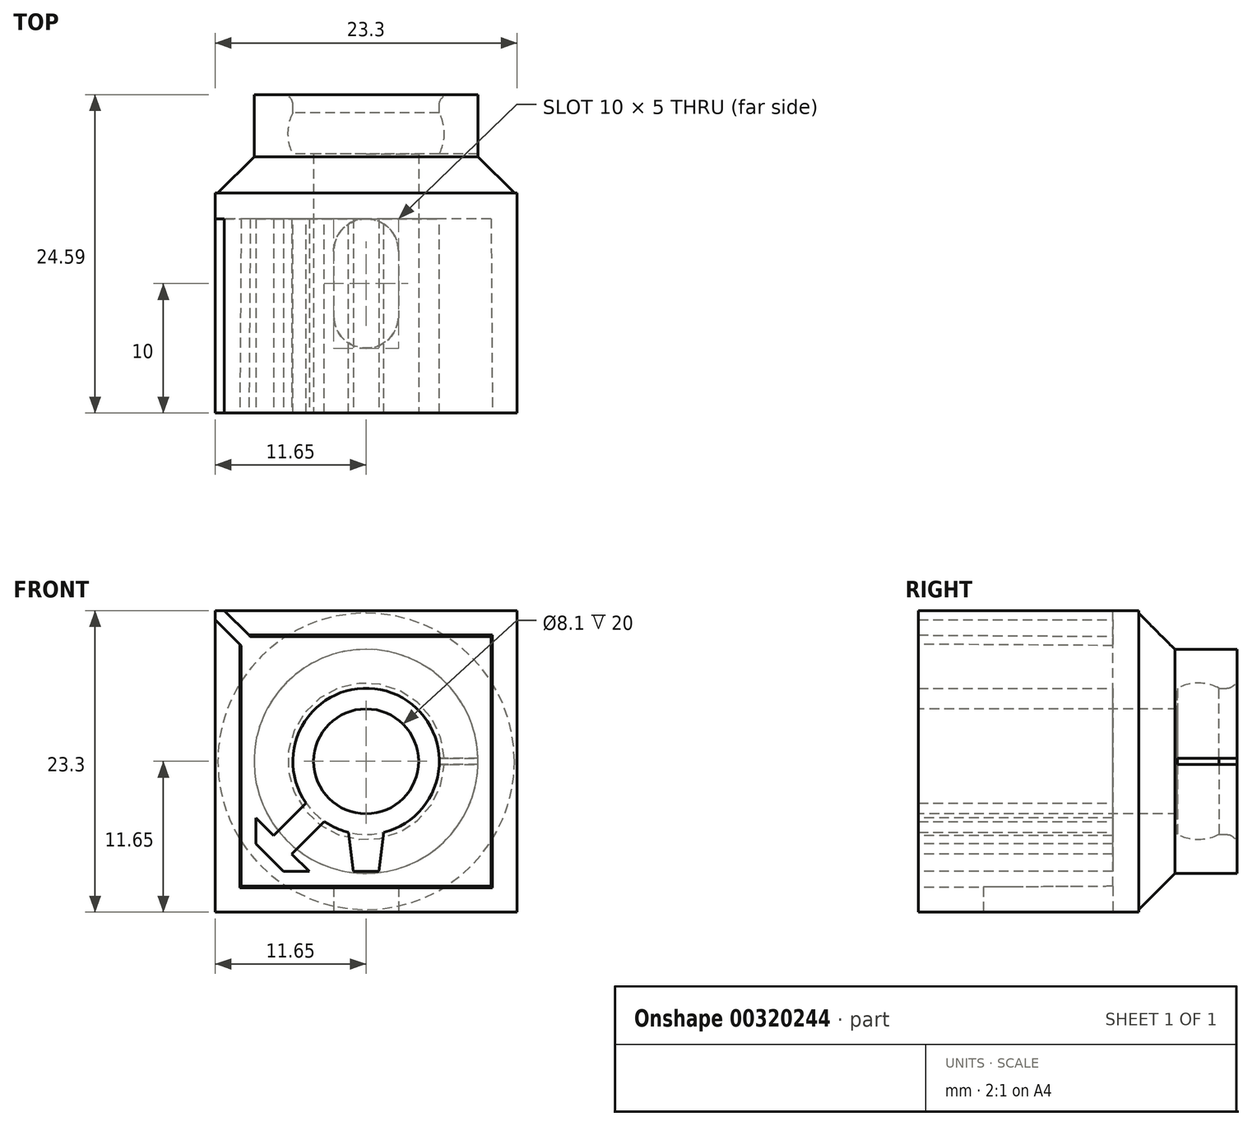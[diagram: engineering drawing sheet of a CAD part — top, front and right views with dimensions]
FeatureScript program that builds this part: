
annotation { "Feature Type Name" : "Feature", "Feature Type Description" : "" }
export const myFeature = defineFeature(function(context is Context, id is Id, definition is map)
    precondition{}
    {
        {
            var Q0;
            Q0=qCreatedBy(makeId("Front.planeOp"),FACE);
            var sketch = newSketch(context, id + "F0", { "sketchPlane" : qUnion([Q0])});
            skLineSegment(sketch, "E0.bottom", {"start": v(9.5, -9.5) * mm, "end": v(-9.5, -9.5) * mm, "construction": true});
            skLineSegment(sketch, "E0.top", {"start": v(9.5, 9.5) * mm, "end": v(-9.5, 9.5) * mm, "construction": true});
            skLineSegment(sketch, "E0.left", {"start": v(9.5, -9.5) * mm, "end": v(9.5, 9.5) * mm, "construction": true});
            skLineSegment(sketch, "E0.right", {"start": v(-9.5, -9.5) * mm, "end": v(-9.5, 9.5) * mm, "construction": true});
            skPoint(sketch, "E0.middle", {"position": v(0, 0) * mm});
            skLineSegment(sketch, "E1.0", {"start": v(8.5, 8.5) * mm, "end": v(-8.5, 8.5) * mm, "construction": true});
            skLineSegment(sketch, "E1.1", {"start": v(8.5, -8.5) * mm, "end": v(8.5, 8.5) * mm, "construction": true});
            skLineSegment(sketch, "E1.2", {"start": v(8.5, -8.5) * mm, "end": v(-8.5, -8.5) * mm, "construction": true});
            skLineSegment(sketch, "E1.3", {"start": v(-8.5, -8.5) * mm, "end": v(-8.5, 8.5) * mm, "construction": true});
            skSolve(sketch);
        }
        {
            var Q0;
            Q0=qCreatedBy(makeId("Front.planeOp"),FACE);
            var sketch = newSketch(context, id + "F1", { "sketchPlane" : qUnion([Q0])});
            skLineSegment(sketch, "E2.0", {"start": v(8.4, 8.4) * mm, "end": v(-8.4, 8.4) * mm});
            skLineSegment(sketch, "E2.1", {"start": v(8.4, -8.4) * mm, "end": v(8.4, 8.4) * mm});
            skLineSegment(sketch, "E2.2", {"start": v(8.4, -8.4) * mm, "end": v(-8.4, -8.4) * mm});
            skLineSegment(sketch, "E2.3", {"start": v(-8.4, -8.4) * mm, "end": v(-8.4, 8.4) * mm});
            skLineSegment(sketch, "E3.0", {"start": v(9.65, 9.65) * mm, "end": v(-9.65, 9.65) * mm});
            skLineSegment(sketch, "E3.1", {"start": v(9.65, -9.65) * mm, "end": v(9.65, 9.65) * mm});
            skLineSegment(sketch, "E3.2", {"start": v(9.65, -9.65) * mm, "end": v(-9.65, -9.65) * mm});
            skLineSegment(sketch, "E3.3", {"start": v(-9.65, -9.65) * mm, "end": v(-9.65, 9.65) * mm});
            skLineSegment(sketch, "E4.0", {"start": v(11.65, 11.65) * mm, "end": v(-11.65, 11.65) * mm});
            skLineSegment(sketch, "E4.1", {"start": v(11.65, -11.65) * mm, "end": v(11.65, 11.65) * mm});
            skLineSegment(sketch, "E4.2", {"start": v(11.65, -11.65) * mm, "end": v(-11.65, -11.65) * mm});
            skLineSegment(sketch, "E4.3", {"start": v(-11.65, -11.65) * mm, "end": v(-11.65, 11.65) * mm});
            skLineSegment(sketch, "E5.0", {"start": v(6.4, 6.4) * mm, "end": v(-6.4, 6.4) * mm});
            skLineSegment(sketch, "E5.1", {"start": v(6.4, -6.4) * mm, "end": v(6.4, 6.4) * mm});
            skLineSegment(sketch, "E5.2", {"start": v(6.4, -6.4) * mm, "end": v(-6.4, -6.4) * mm});
            skLineSegment(sketch, "E5.3", {"start": v(-6.4, -6.4) * mm, "end": v(-6.4, 6.4) * mm});
            skSolve(sketch);
        }
        {
            var Q0;
            Q0=makeQuery(id+"F1.imprint","IMPRINT",FACE,{"disambiguationData":[TD([[makeQuery(id+"F1.imprint","IMPRINT",EDGE,{"derivedFrom":sQuery(id+"F1.wireOp",EDGE,"E3.0")}),-1.0]])]});
            extrude(context, id + "F2", {"entities" : qUnion([Q0]), "oppositeDirection" : true, "depth" : 25 * mm});
        }
        {
            var Q0;
            Q0=makeQuery(id+"F2.opExtrude","CAP_FACE",FACE,{"disambiguationData":[OSD([sQuery(id+"F1.wireOp",EDGE,"E3.0"),sQuery(id+"F1.wireOp",EDGE,"E3.1"),sQuery(id+"F1.wireOp",EDGE,"E3.2"),sQuery(id+"F1.wireOp",EDGE,"E3.3"),sQuery(id+"F1.wireOp",EDGE,"E4.0"),sQuery(id+"F1.wireOp",EDGE,"E4.1"),sQuery(id+"F1.wireOp",EDGE,"E4.2"),sQuery(id+"F1.wireOp",EDGE,"E4.3")])],"isStart":true});
            var sketch = newSketch(context, id + "F3", { "sketchPlane" : qUnion([Q0])});
            skLineSegment(sketch, "E6.0.0", {"start": v(-11.65, 11.65) * mm, "end": v(-11.65, -11.65) * mm});
            skLineSegment(sketch, "E6.0.1", {"start": v(-11.65, -11.65) * mm, "end": v(11.65, -11.65) * mm});
            skLineSegment(sketch, "E6.0.2", {"start": v(11.65, -11.65) * mm, "end": v(11.65, 11.65) * mm});
            skLineSegment(sketch, "E6.0.3", {"start": v(11.65, 11.65) * mm, "end": v(-11.65, 11.65) * mm});
            skSolve(sketch);
        }
        {
            var Q0;
            Q0=qSketchRegion(id+"F3",true);
            extrude(context, id + "F4", {"entities" : qUnion([Q0]), "operationType" : NewBodyOperationType.ADD, "oppositeDirection" : true, "depth" : 3 * mm});
        }
        {
            var Q0;
            Q0=makeQuery(id+"F4.boolean.opBoolean","MERGE",FACE,{"derivedFrom":[makeQuery(id+"F2.opExtrude","CAP_FACE",FACE,{"disambiguationData":[OSD([sQuery(id+"F1.wireOp",EDGE,"E2.0"),sQuery(id+"F1.wireOp",EDGE,"E2.1"),sQuery(id+"F1.wireOp",EDGE,"E2.2"),sQuery(id+"F1.wireOp",EDGE,"E2.3"),sQuery(id+"F1.wireOp",EDGE,"E5.0"),sQuery(id+"F1.wireOp",EDGE,"E5.1"),sQuery(id+"F1.wireOp",EDGE,"E5.2"),sQuery(id+"F1.wireOp",EDGE,"E5.3")])],"isStart":true}),makeQuery(id+"F2.opExtrude","CAP_FACE",FACE,{"disambiguationData":[OSD([sQuery(id+"F1.wireOp",EDGE,"E3.0"),sQuery(id+"F1.wireOp",EDGE,"E3.1"),sQuery(id+"F1.wireOp",EDGE,"E3.2"),sQuery(id+"F1.wireOp",EDGE,"E3.3"),sQuery(id+"F1.wireOp",EDGE,"E4.0"),sQuery(id+"F1.wireOp",EDGE,"E4.1"),sQuery(id+"F1.wireOp",EDGE,"E4.2"),sQuery(id+"F1.wireOp",EDGE,"E4.3")])],"isStart":true}),makeQuery(id+"F4.opExtrude","CAP_FACE",FACE,{"disambiguationData":[OSD([sQuery(id+"F3.wireOp",EDGE,"E6.0.0"),sQuery(id+"F3.wireOp",EDGE,"E6.0.1"),sQuery(id+"F3.wireOp",EDGE,"E6.0.2"),sQuery(id+"F3.wireOp",EDGE,"E6.0.3")])],"isStart":true})]});
            var sketch = newSketch(context, id + "F5", { "sketchPlane" : qUnion([Q0])});
            skCircle(sketch, "E7", {"center": v(0, 0) * mm, "radius": 4.05 * mm});
            skSolve(sketch);
        }
        {
            var Q0;
            Q0=qSketchRegion(id+"F5",true);
            extrude(context, id + "F6", {"entities" : qUnion([Q0]), "operationType" : NewBodyOperationType.REMOVE, "endBound" : BoundingType.THROUGH_ALL, "oppositeDirection" : true, "depth" : 25 * mm});
        }
        {
            var Q0;
            Q0=qCreatedBy(makeId("Right.planeOp"),FACE);
            var sketch = newSketch(context, id + "F7", { "sketchPlane" : qUnion([Q0])});
            skLineSegment(sketch, "E8.bottom", {"start": v(3, -4.05) * mm, "end": v(20, -4.05) * mm});
            skLineSegment(sketch, "E8.top", {"start": v(3, -5.65) * mm, "end": v(20, -5.65) * mm});
            skLineSegment(sketch, "E8.left", {"start": v(3, -4.05) * mm, "end": v(3, -5.65) * mm});
            skLineSegment(sketch, "E8.right", {"start": v(20, -4.05) * mm, "end": v(20, -5.65) * mm});
            skArc(sketch, "E9", {"start": v(20, -5.65) * mm, "mid": v(21.6, -6.05) * mm, "end": v(23.2, -5.65) * mm});
            skLineSegment(sketch, "E10", {"start": v(23.2, -5.65) * mm, "end": v(26.09, -5.65) * mm});
            skArc(sketch, "E11.0", {"start": v(17.11, -5.65) * mm, "mid": v(21.6, -8.05) * mm, "end": v(26.09, -5.65) * mm});
            skLineSegment(sketch, "E12", {"start": v(24.82, -8.05) * mm, "end": v(16.07, -8.05) * mm, "construction": true});
            skSolve(sketch);
        }
        {
            var Q0;
            Q0=qSketchRegion(id+"F7",true);
            var Q1;
            Q1=makeQuery(id+"F6.boolean.opBoolean","INTERSECT",EDGE,{"derivedFrom":[makeQuery(id+"F4.opExtrude","CAP_FACE",FACE,{"disambiguationData":[OSD([sQuery(id+"F3.wireOp",EDGE,"E6.0.0"),sQuery(id+"F3.wireOp",EDGE,"E6.0.1"),sQuery(id+"F3.wireOp",EDGE,"E6.0.2"),sQuery(id+"F3.wireOp",EDGE,"E6.0.3")])],"isStart":false}),makeQuery(id+"F6.opExtrude","SWEPT_FACE",FACE,{"disambiguationData":[OSD([sQuery(id+"F5.wireOp",EDGE,"E7")])]})]});
            revolve(context, id + "F8", {"operationType" : NewBodyOperationType.ADD, "entities" : qUnion([Q0]), "axis" : qUnion([Q1]), "revolveType" : RevolveType.FULL});
        }
        {
            var Q0;
            Q0=makeQuery(id+"F2.opExtrude","CAP_FACE",FACE,{"disambiguationData":[OSD([sQuery(id+"F1.wireOp",EDGE,"E3.0"),sQuery(id+"F1.wireOp",EDGE,"E3.1"),sQuery(id+"F1.wireOp",EDGE,"E3.2"),sQuery(id+"F1.wireOp",EDGE,"E3.3"),sQuery(id+"F1.wireOp",EDGE,"E4.0"),sQuery(id+"F1.wireOp",EDGE,"E4.1"),sQuery(id+"F1.wireOp",EDGE,"E4.2"),sQuery(id+"F1.wireOp",EDGE,"E4.3")])],"isStart":false});
            cPlane(context, id + "F9", {"entities" : qUnion([Q0]), "cplaneType" : CPlaneType.OFFSET, "offset" : 8 * mm, "oppositeDirection" : true, "width" : 150 * mm, "height" : 150 * mm});
        }
        {
            var Q0;
            Q0=qCreatedBy(id+"F9.planeOp",FACE);
            var sketch = newSketch(context, id + "F10", { "sketchPlane" : qUnion([Q0])});
            skLineSegment(sketch, "E13.0.0", {"start": v(11.65, -11.65) * mm, "end": v(11.65, 11.65) * mm});
            skLineSegment(sketch, "E13.0.1", {"start": v(11.65, 11.65) * mm, "end": v(-11.65, 11.65) * mm});
            skLineSegment(sketch, "E13.0.2", {"start": v(-11.65, 11.65) * mm, "end": v(-11.65, -11.65) * mm});
            skLineSegment(sketch, "E13.0.3", {"start": v(-11.65, -11.65) * mm, "end": v(11.65, -11.65) * mm});
            skSolve(sketch);
        }
        {
            var Q0;
            Q0=qSketchRegion(id+"F10",true);
            extrude(context, id + "F11", {"entities" : qUnion([Q0]), "oppositeDirection" : true, "depth" : 2 * mm});
        }
        {
            var Q0;
            Q0=makeQuery(id+"F2.opExtrude","SWEPT_BODY",BODY,{"disambiguationData":[OSD([sQuery(id+"F1.wireOp",EDGE,"E3.0"),sQuery(id+"F1.wireOp",EDGE,"E3.1"),sQuery(id+"F1.wireOp",EDGE,"E3.2"),sQuery(id+"F1.wireOp",EDGE,"E3.3"),sQuery(id+"F1.wireOp",EDGE,"E4.0"),sQuery(id+"F1.wireOp",EDGE,"E4.1"),sQuery(id+"F1.wireOp",EDGE,"E4.2"),sQuery(id+"F1.wireOp",EDGE,"E4.3")])]});
            var Q1;
            Q1=makeQuery(id+"F11.opExtrude","SWEPT_BODY",BODY,{"disambiguationData":[OSD([sQuery(id+"F10.wireOp",EDGE,"E13.0.0"),sQuery(id+"F10.wireOp",EDGE,"E13.0.1"),sQuery(id+"F10.wireOp",EDGE,"E13.0.2"),sQuery(id+"F10.wireOp",EDGE,"E13.0.3")])]});
            booleanBodies(context, id + "F12", {"operationType" : BooleanOperationType.UNION, "tools" : qUnion([Q0, Q1])});
        }
        {
            var Q0;
            Q0=makeQuery(id+"F12.opBoolean","SPLIT",FACE,{"disambiguationData":[TD([makeQuery(id+"F6.boolean.opBoolean","COPY",FACE,{"derivedFrom":makeQuery(id+"F6.opExtrude","SWEPT_FACE",FACE,{"disambiguationData":[OSD([sQuery(id+"F5.wireOp",EDGE,"E7")])]})})])],"derivedFrom":makeQuery(id+"F11.opExtrude","CAP_FACE",FACE,{"disambiguationData":[OSD([sQuery(id+"F10.wireOp",EDGE,"E13.0.0"),sQuery(id+"F10.wireOp",EDGE,"E13.0.1"),sQuery(id+"F10.wireOp",EDGE,"E13.0.2"),sQuery(id+"F10.wireOp",EDGE,"E13.0.3")])],"isStart":true})});
            var sketch = newSketch(context, id + "F13", { "sketchPlane" : qUnion([Q0])});
            skCircle(sketch, "E14.0", {"center": v(0, 0) * mm, "radius": 4.05 * mm});
            skSolve(sketch);
        }
        {
            var Q0;
            Q0=qSketchRegion(id+"F13",true);
            extrude(context, id + "F14", {"entities" : qUnion([Q0]), "operationType" : NewBodyOperationType.REMOVE, "endBound" : BoundingType.THROUGH_ALL, "oppositeDirection" : true, "depth" : 25 * mm});
        }
        {
            var Q0;
            Q0=makeQuery(id+"F4.opExtrude","CAP_FACE",FACE,{"disambiguationData":[OSD([sQuery(id+"F3.wireOp",EDGE,"E6.0.0"),sQuery(id+"F3.wireOp",EDGE,"E6.0.1"),sQuery(id+"F3.wireOp",EDGE,"E6.0.2"),sQuery(id+"F3.wireOp",EDGE,"E6.0.3")])],"isStart":false});
            var sketch = newSketch(context, id + "F15", { "sketchPlane" : qUnion([Q0])});
            skLineSegment(sketch, "E15.0.0", {"start": v(-9.65, -9.65) * mm, "end": v(9.65, -9.65) * mm});
            skLineSegment(sketch, "E15.0.1", {"start": v(9.65, -9.65) * mm, "end": v(9.65, 9.65) * mm});
            skLineSegment(sketch, "E15.0.2", {"start": v(9.65, 9.65) * mm, "end": v(-9.65, 9.65) * mm});
            skLineSegment(sketch, "E15.0.3", {"start": v(-9.65, 9.65) * mm, "end": v(-9.65, -9.65) * mm});
            skCircle(sketch, "E16.0", {"center": v(0, 0) * mm, "radius": 5.65 * mm});
            skSolve(sketch);
        }
        {
            var Q0;
            Q0=qSketchRegion(id+"F15",true);
            extrude(context, id + "F16", {"entities" : qUnion([Q0]), "operationType" : NewBodyOperationType.REMOVE, "endBound" : BoundingType.THROUGH_ALL, "oppositeDirection" : true, "depth" : 25 * mm});
        }
        {
            var Q0;
            Q0=makeQuery(id+"F12.opBoolean","SPLIT",FACE,{"disambiguationData":[TD([makeQuery(id+"F2.opExtrude","SWEPT_FACE",FACE,{"disambiguationData":[OSD([sQuery(id+"F1.wireOp",EDGE,"E3.0")])]})])],"derivedFrom":makeQuery(id+"F11.opExtrude","CAP_FACE",FACE,{"disambiguationData":[OSD([sQuery(id+"F10.wireOp",EDGE,"E13.0.0"),sQuery(id+"F10.wireOp",EDGE,"E13.0.1"),sQuery(id+"F10.wireOp",EDGE,"E13.0.2"),sQuery(id+"F10.wireOp",EDGE,"E13.0.3")])],"isStart":false})});
            var sketch = newSketch(context, id + "F17", { "sketchPlane" : qUnion([Q0])});
            skLineSegment(sketch, "E17.0", {"start": v(9.5, -9.5) * mm, "end": v(-9.5, -9.5) * mm});
            skLineSegment(sketch, "E17.1", {"start": v(9.5, 9.5) * mm, "end": v(-9.5, 9.5) * mm});
            skLineSegment(sketch, "E17.2", {"start": v(9.5, -9.5) * mm, "end": v(9.5, 9.5) * mm});
            skLineSegment(sketch, "E17.3", {"start": v(-9.5, -9.5) * mm, "end": v(-9.5, 9.5) * mm});
            skPoint(sketch, "E17.4", {"position": v(0, 0) * mm});
            skLineSegment(sketch, "E17.5", {"start": v(8.5, 8.5) * mm, "end": v(-8.5, 8.5) * mm});
            skLineSegment(sketch, "E17.6", {"start": v(8.5, -8.5) * mm, "end": v(8.5, 8.5) * mm});
            skLineSegment(sketch, "E17.7", {"start": v(8.5, -8.5) * mm, "end": v(-8.5, -8.5) * mm});
            skLineSegment(sketch, "E17.8", {"start": v(-8.5, -8.5) * mm, "end": v(-8.5, 8.5) * mm});
            skSolve(sketch);
        }
        {
            var Q0;
            {var subQ0=sQuery(id+"F1.wireOp",EDGE,"E4.3");var subQ1=sQuery(id+"F1.wireOp",EDGE,"E4.2");var subQ2=sQuery(id+"F1.wireOp",EDGE,"E4.1");var subQ3=sQuery(id+"F1.wireOp",EDGE,"E4.0");var subQ4=sQuery(id+"F1.wireOp",EDGE,"E3.0");var subQ5=sQuery(id+"F1.wireOp",EDGE,"E3.3");var subQ6=sQuery(id+"F1.wireOp",EDGE,"E3.1");var subQ7=sQuery(id+"F1.wireOp",EDGE,"E3.2");Q0=makeQuery(id+"F16.boolean.opBoolean","SPLIT",FACE,{"disambiguationData":[TD([makeQuery(id+"F2.opExtrude","SWEPT_FACE",FACE,{"disambiguationData":[OSD([subQ4])]})])],"derivedFrom":makeQuery(id+"F4.boolean.opBoolean","MERGE",FACE,{"derivedFrom":[makeQuery(id+"F2.opExtrude","CAP_FACE",FACE,{"disambiguationData":[OSD([subQ4,subQ6,subQ7,subQ5,subQ3,subQ2,subQ1,subQ0])],"isStart":true}),makeQuery(id+"F4.opExtrude","CAP_FACE",FACE,{"disambiguationData":[OSD([sQuery(id+"F3.wireOp",EDGE,"E6.0.0"),sQuery(id+"F3.wireOp",EDGE,"E6.0.1"),sQuery(id+"F3.wireOp",EDGE,"E6.0.2"),sQuery(id+"F3.wireOp",EDGE,"E6.0.3")])],"isStart":true})]})});}
            var sketch = newSketch(context, id + "F18", { "sketchPlane" : qUnion([Q0])});
            skLineSegment(sketch, "E18", {"start": v(1.5, -4.5) * mm, "end": v(0.97, -8.5) * mm});
            skLineSegment(sketch, "E19", {"start": v(-0.97, -8.5) * mm, "end": v(-1.5, -4.5) * mm});
            skLineSegment(sketch, "E20", {"start": v(-1.5, -4.5) * mm, "end": v(1.5, -4.5) * mm});
            skLineSegment(sketch, "E21.0", {"start": v(8.5, -8.5) * mm, "end": v(-8.5, -8.5) * mm, "construction": true});
            skPoint(sketch, "E22.orphan", {"position": v(0, -15.9) * mm});
            skLineSegment(sketch, "E23", {"start": v(-0.97, -8.5) * mm, "end": v(0.97, -8.5) * mm});
            skSolve(sketch);
        }
        {
            var Q0;
            Q0=qSketchRegion(id+"F18",true);
            var Q1;
            Q1=makeQuery(id+"F12.opBoolean","SPLIT",FACE,{"disambiguationData":[TD([makeQuery(id+"F2.opExtrude","SWEPT_FACE",FACE,{"disambiguationData":[OSD([sQuery(id+"F1.wireOp",EDGE,"E3.0")])]})])],"derivedFrom":makeQuery(id+"F11.opExtrude","CAP_FACE",FACE,{"disambiguationData":[OSD([sQuery(id+"F10.wireOp",EDGE,"E13.0.0"),sQuery(id+"F10.wireOp",EDGE,"E13.0.1"),sQuery(id+"F10.wireOp",EDGE,"E13.0.2"),sQuery(id+"F10.wireOp",EDGE,"E13.0.3")])],"isStart":false})});
            extrude(context, id + "F19", {"entities" : qUnion([Q0]), "operationType" : NewBodyOperationType.ADD, "endBound" : BoundingType.UP_TO_SURFACE, "oppositeDirection" : true, "endBoundEntityFace" : qUnion([Q1]), "depth" : 25 * mm});
        }
        {
            var Q0;
            {var subQ0=sQuery(id+"F1.wireOp",EDGE,"E4.3");var subQ1=sQuery(id+"F1.wireOp",EDGE,"E4.2");var subQ2=sQuery(id+"F1.wireOp",EDGE,"E4.1");var subQ3=sQuery(id+"F1.wireOp",EDGE,"E4.0");var subQ4=sQuery(id+"F1.wireOp",EDGE,"E3.0");var subQ5=sQuery(id+"F1.wireOp",EDGE,"E3.3");var subQ6=sQuery(id+"F1.wireOp",EDGE,"E3.1");var subQ7=sQuery(id+"F1.wireOp",EDGE,"E3.2");Q0=makeQuery(id+"F16.boolean.opBoolean","SPLIT",FACE,{"disambiguationData":[TD([makeQuery(id+"F2.opExtrude","SWEPT_FACE",FACE,{"disambiguationData":[OSD([subQ4])]})])],"derivedFrom":makeQuery(id+"F4.boolean.opBoolean","MERGE",FACE,{"derivedFrom":[makeQuery(id+"F2.opExtrude","CAP_FACE",FACE,{"disambiguationData":[OSD([subQ4,subQ6,subQ7,subQ5,subQ3,subQ2,subQ1,subQ0])],"isStart":true}),makeQuery(id+"F4.opExtrude","CAP_FACE",FACE,{"disambiguationData":[OSD([sQuery(id+"F3.wireOp",EDGE,"E6.0.0"),sQuery(id+"F3.wireOp",EDGE,"E6.0.1"),sQuery(id+"F3.wireOp",EDGE,"E6.0.2"),sQuery(id+"F3.wireOp",EDGE,"E6.0.3")])],"isStart":true})]})});}
            var sketch = newSketch(context, id + "F20", { "sketchPlane" : qUnion([Q0])});
            skLineSegment(sketch, "E24", {"start": v(-6.38, -8.5) * mm, "end": v(-8.5, -6.38) * mm});
            skLineSegment(sketch, "E25.0", {"start": v(-8.5, -6.38) * mm, "end": v(-8.5, -4.38) * mm});
            skLineSegment(sketch, "E26.0", {"start": v(-4.38, -8.5) * mm, "end": v(-6.38, -8.5) * mm});
            skCircle(sketch, "E27.0", {"center": v(0, 0) * mm, "radius": 4.05 * mm});
            skPoint(sketch, "E28.orphan", {"position": v(-8.5, 8.5) * mm});
            skPoint(sketch, "E29.orphan", {"position": v(8.5, -8.5) * mm});
            skPoint(sketch, "E30.orphan", {"position": v(-8.5, -8.5) * mm});
            skLineSegment(sketch, "E31", {"start": v(-8.5, -4.38) * mm, "end": v(-4.38, -8.5) * mm});
            skLineSegment(sketch, "E32", {"start": v(-6.44, -6.44) * mm, "end": v(0, 0) * mm, "construction": true});
            skLineSegment(sketch, "E33.0", {"start": v(-5.73, -7.15) * mm, "end": v(-2.07, -3.48) * mm});
            skLineSegment(sketch, "E34.0", {"start": v(-7.15, -5.73) * mm, "end": v(-3.48, -2.07) * mm});
            skSolve(sketch);
        }
        {
            var Q0;
            Q0=makeQuery(id+"F20.imprint","IMPRINT",FACE,{"disambiguationData":[TD([[makeQuery(id+"F20.imprint","IMPRINT",EDGE,{"derivedFrom":sQuery(id+"F20.wireOp",EDGE,"E24")}),-1.0]])]});
            var Q1;
            {var subQ0=sQuery(id+"F20.wireOp",EDGE,"E33.0");Q1=makeQuery(id+"F20.imprint","IMPRINT",FACE,{"disambiguationData":[TD([[makeQuery(id+"F20.imprint","IMPRINT",EDGE,{"derivedFrom":subQ0}),1.0]])]});}
            var Q2;
            Q2=makeQuery(id+"F12.opBoolean","SPLIT",FACE,{"disambiguationData":[TD([makeQuery(id+"F2.opExtrude","SWEPT_FACE",FACE,{"disambiguationData":[OSD([sQuery(id+"F1.wireOp",EDGE,"E3.0")])]})])],"derivedFrom":makeQuery(id+"F11.opExtrude","CAP_FACE",FACE,{"disambiguationData":[OSD([sQuery(id+"F10.wireOp",EDGE,"E13.0.0"),sQuery(id+"F10.wireOp",EDGE,"E13.0.1"),sQuery(id+"F10.wireOp",EDGE,"E13.0.2"),sQuery(id+"F10.wireOp",EDGE,"E13.0.3")])],"isStart":false})});
            extrude(context, id + "F21", {"entities" : qUnion([Q0, Q1]), "operationType" : NewBodyOperationType.ADD, "endBound" : BoundingType.UP_TO_SURFACE, "oppositeDirection" : true, "endBoundEntityFace" : qUnion([Q2]), "depth" : 25 * mm});
        }
        {
            var Q0;
            Q0=makeQuery(id+"F16.boolean.opBoolean","INTERSECT",EDGE,{"derivedFrom":[makeQuery(id+"F4.boolean.opBoolean","MERGE",FACE,{"derivedFrom":[makeQuery(id+"F2.opExtrude","CAP_FACE",FACE,{"disambiguationData":[OSD([sQuery(id+"F1.wireOp",EDGE,"E3.0"),sQuery(id+"F1.wireOp",EDGE,"E3.1"),sQuery(id+"F1.wireOp",EDGE,"E3.2"),sQuery(id+"F1.wireOp",EDGE,"E3.3"),sQuery(id+"F1.wireOp",EDGE,"E4.0"),sQuery(id+"F1.wireOp",EDGE,"E4.1"),sQuery(id+"F1.wireOp",EDGE,"E4.2"),sQuery(id+"F1.wireOp",EDGE,"E4.3")])],"isStart":true}),makeQuery(id+"F4.opExtrude","CAP_FACE",FACE,{"disambiguationData":[OSD([sQuery(id+"F3.wireOp",EDGE,"E6.0.0"),sQuery(id+"F3.wireOp",EDGE,"E6.0.1"),sQuery(id+"F3.wireOp",EDGE,"E6.0.2"),sQuery(id+"F3.wireOp",EDGE,"E6.0.3")])],"isStart":true})]}),makeQuery(id+"F16.opExtrude","SWEPT_FACE",FACE,{"disambiguationData":[OSD([sQuery(id+"F15.wireOp",EDGE,"E15.0.0")])]})]});
            var Q1;
            Q1=makeQuery(id+"F16.boolean.opBoolean","INTERSECT",EDGE,{"derivedFrom":[makeQuery(id+"F4.boolean.opBoolean","MERGE",FACE,{"derivedFrom":[makeQuery(id+"F2.opExtrude","CAP_FACE",FACE,{"disambiguationData":[OSD([sQuery(id+"F1.wireOp",EDGE,"E3.0"),sQuery(id+"F1.wireOp",EDGE,"E3.1"),sQuery(id+"F1.wireOp",EDGE,"E3.2"),sQuery(id+"F1.wireOp",EDGE,"E3.3"),sQuery(id+"F1.wireOp",EDGE,"E4.0"),sQuery(id+"F1.wireOp",EDGE,"E4.1"),sQuery(id+"F1.wireOp",EDGE,"E4.2"),sQuery(id+"F1.wireOp",EDGE,"E4.3")])],"isStart":true}),makeQuery(id+"F4.opExtrude","CAP_FACE",FACE,{"disambiguationData":[OSD([sQuery(id+"F3.wireOp",EDGE,"E6.0.0"),sQuery(id+"F3.wireOp",EDGE,"E6.0.1"),sQuery(id+"F3.wireOp",EDGE,"E6.0.2"),sQuery(id+"F3.wireOp",EDGE,"E6.0.3")])],"isStart":true})]}),makeQuery(id+"F16.opExtrude","SWEPT_FACE",FACE,{"disambiguationData":[OSD([sQuery(id+"F15.wireOp",EDGE,"E15.0.3")])]})]});
            var Q2;
            Q2=makeQuery(id+"F16.boolean.opBoolean","INTERSECT",EDGE,{"derivedFrom":[makeQuery(id+"F4.boolean.opBoolean","MERGE",FACE,{"derivedFrom":[makeQuery(id+"F2.opExtrude","CAP_FACE",FACE,{"disambiguationData":[OSD([sQuery(id+"F1.wireOp",EDGE,"E3.0"),sQuery(id+"F1.wireOp",EDGE,"E3.1"),sQuery(id+"F1.wireOp",EDGE,"E3.2"),sQuery(id+"F1.wireOp",EDGE,"E3.3"),sQuery(id+"F1.wireOp",EDGE,"E4.0"),sQuery(id+"F1.wireOp",EDGE,"E4.1"),sQuery(id+"F1.wireOp",EDGE,"E4.2"),sQuery(id+"F1.wireOp",EDGE,"E4.3")])],"isStart":true}),makeQuery(id+"F4.opExtrude","CAP_FACE",FACE,{"disambiguationData":[OSD([sQuery(id+"F3.wireOp",EDGE,"E6.0.0"),sQuery(id+"F3.wireOp",EDGE,"E6.0.1"),sQuery(id+"F3.wireOp",EDGE,"E6.0.2"),sQuery(id+"F3.wireOp",EDGE,"E6.0.3")])],"isStart":true})]}),makeQuery(id+"F16.opExtrude","SWEPT_FACE",FACE,{"disambiguationData":[OSD([sQuery(id+"F15.wireOp",EDGE,"E15.0.1")])]})]});
            var Q3;
            Q3=makeQuery(id+"F16.boolean.opBoolean","INTERSECT",EDGE,{"derivedFrom":[makeQuery(id+"F4.boolean.opBoolean","MERGE",FACE,{"derivedFrom":[makeQuery(id+"F2.opExtrude","CAP_FACE",FACE,{"disambiguationData":[OSD([sQuery(id+"F1.wireOp",EDGE,"E3.0"),sQuery(id+"F1.wireOp",EDGE,"E3.1"),sQuery(id+"F1.wireOp",EDGE,"E3.2"),sQuery(id+"F1.wireOp",EDGE,"E3.3"),sQuery(id+"F1.wireOp",EDGE,"E4.0"),sQuery(id+"F1.wireOp",EDGE,"E4.1"),sQuery(id+"F1.wireOp",EDGE,"E4.2"),sQuery(id+"F1.wireOp",EDGE,"E4.3")])],"isStart":true}),makeQuery(id+"F4.opExtrude","CAP_FACE",FACE,{"disambiguationData":[OSD([sQuery(id+"F3.wireOp",EDGE,"E6.0.0"),sQuery(id+"F3.wireOp",EDGE,"E6.0.1"),sQuery(id+"F3.wireOp",EDGE,"E6.0.2"),sQuery(id+"F3.wireOp",EDGE,"E6.0.3")])],"isStart":true})]}),makeQuery(id+"F16.opExtrude","SWEPT_FACE",FACE,{"disambiguationData":[OSD([sQuery(id+"F15.wireOp",EDGE,"E15.0.2")])]})]});
            chamfer(context, id + "F22", {"entities" : qUnion([Q0, Q1, Q2, Q3]), "chamferType" : ChamferType.TWO_OFFSETS, "width1" : .1 * mm, "oppositeDirection" : false, "width2" : 15 * mm, "tangentPropagation" : true});
        }
        {
            var Q0;
            Q0=makeQuery(id+"F2.opExtrude","SWEPT_FACE",FACE,{"disambiguationData":[OSD([sQuery(id+"F1.wireOp",EDGE,"E4.2")])]});
            var sketch = newSketch(context, id + "F23", { "sketchPlane" : qUnion([Q0])});
            skLineSegment(sketch, "E35.bottom", {"start": v(2.5, -15) * mm, "end": v(-2.5, -15) * mm});
            skLineSegment(sketch, "E35.top", {"start": v(2.5, -5) * mm, "end": v(-2.5, -5) * mm});
            skLineSegment(sketch, "E35.left", {"start": v(2.5, -15) * mm, "end": v(2.5, -5) * mm});
            skLineSegment(sketch, "E35.right", {"start": v(-2.5, -15) * mm, "end": v(-2.5, -5) * mm});
            skPoint(sketch, "E35.middle", {"position": v(0, -10) * mm});
            skSolve(sketch);
        }
        {
            var Q0;
            Q0=qSketchRegion(id+"F23",true);
            extrude(context, id + "F24", {"entities" : qUnion([Q0]), "operationType" : NewBodyOperationType.REMOVE, "oppositeDirection" : true, "depth" : 2.5 * mm});
        }
        {
            var Q0;
            Q0=makeQuery(id+"F24.boolean.opBoolean","COPY",EDGE,{"derivedFrom":makeQuery(id+"F24.opExtrude","SWEPT_EDGE",EDGE,{"disambiguationData":[OSD([sQuery(id+"F23.wireOp",EDGE,"E35.top"),sQuery(id+"F23.wireOp",EDGE,"E35.right")])]})});
            var Q1;
            Q1=makeQuery(id+"F24.boolean.opBoolean","COPY",EDGE,{"derivedFrom":makeQuery(id+"F24.opExtrude","SWEPT_EDGE",EDGE,{"disambiguationData":[OSD([sQuery(id+"F23.wireOp",EDGE,"E35.top"),sQuery(id+"F23.wireOp",EDGE,"E35.left")])]})});
            var Q2;
            Q2=makeQuery(id+"F24.boolean.opBoolean","COPY",EDGE,{"derivedFrom":makeQuery(id+"F24.opExtrude","SWEPT_EDGE",EDGE,{"disambiguationData":[OSD([sQuery(id+"F23.wireOp",EDGE,"E35.bottom"),sQuery(id+"F23.wireOp",EDGE,"E35.right")])]})});
            var Q3;
            Q3=makeQuery(id+"F24.boolean.opBoolean","COPY",EDGE,{"derivedFrom":makeQuery(id+"F24.opExtrude","SWEPT_EDGE",EDGE,{"disambiguationData":[OSD([sQuery(id+"F23.wireOp",EDGE,"E35.bottom"),sQuery(id+"F23.wireOp",EDGE,"E35.left")])]})});
            fillet(context, id + "F25", {"entities" : qUnion([Q0, Q1, Q2, Q3]), "radius" : 2.5 * mm, "tangentPropagation" : true, "allowEdgeOverflow" : false});
        }
        {
            var Q0;
            Q0=makeQuery(id+"F2.opExtrude","CAP_FACE",FACE,{"disambiguationData":[OSD([sQuery(id+"F1.wireOp",EDGE,"E3.0"),sQuery(id+"F1.wireOp",EDGE,"E3.1"),sQuery(id+"F1.wireOp",EDGE,"E3.2"),sQuery(id+"F1.wireOp",EDGE,"E3.3"),sQuery(id+"F1.wireOp",EDGE,"E4.0"),sQuery(id+"F1.wireOp",EDGE,"E4.1"),sQuery(id+"F1.wireOp",EDGE,"E4.2"),sQuery(id+"F1.wireOp",EDGE,"E4.3")])],"isStart":false});
            var sketch = newSketch(context, id + "F26", { "sketchPlane" : qUnion([Q0])});
            skLineSegment(sketch, "E36.0.0", {"start": v(11.65, -11.65) * mm, "end": v(11.65, 11.65) * mm});
            skLineSegment(sketch, "E36.0.1", {"start": v(11.65, 11.65) * mm, "end": v(-11.65, 11.65) * mm});
            skLineSegment(sketch, "E36.0.2", {"start": v(-11.65, 11.65) * mm, "end": v(-11.65, -11.65) * mm});
            skLineSegment(sketch, "E36.0.3", {"start": v(-11.65, -11.65) * mm, "end": v(11.65, -11.65) * mm});
            skLineSegment(sketch, "E37.0", {"start": v(-9.65, -9.65) * mm, "end": v(9.65, -9.65) * mm});
            skLineSegment(sketch, "E38.0", {"start": v(-9.65, -9.65) * mm, "end": v(-9.65, 9.65) * mm});
            skLineSegment(sketch, "E39.0", {"start": v(-9.65, 9.65) * mm, "end": v(9.65, 9.65) * mm});
            skLineSegment(sketch, "E40.0", {"start": v(9.65, -9.65) * mm, "end": v(9.65, 9.65) * mm});
            skSolve(sketch);
        }
        {
            var Q0;
            Q0=qSketchRegion(id+"F26",true);
            var Q1;
            Q1=makeQuery(id+"F12.opBoolean","SPLIT",FACE,{"disambiguationData":[TD([makeQuery(id+"F2.opExtrude","SWEPT_FACE",FACE,{"disambiguationData":[OSD([sQuery(id+"F1.wireOp",EDGE,"E3.0")])]})])],"derivedFrom":makeQuery(id+"F11.opExtrude","CAP_FACE",FACE,{"disambiguationData":[OSD([sQuery(id+"F10.wireOp",EDGE,"E13.0.0"),sQuery(id+"F10.wireOp",EDGE,"E13.0.1"),sQuery(id+"F10.wireOp",EDGE,"E13.0.2"),sQuery(id+"F10.wireOp",EDGE,"E13.0.3")])],"isStart":true})});
            extrude(context, id + "F27", {"entities" : qUnion([Q0]), "operationType" : NewBodyOperationType.REMOVE, "endBound" : BoundingType.UP_TO_SURFACE, "oppositeDirection" : true, "endBoundEntityFace" : qUnion([Q1]), "depth" : 25 * mm});
        }
        {
            var Q0;
            Q0=qCreatedBy(makeId("Right.planeOp"),FACE);
            var sketch = newSketch(context, id + "F28", { "sketchPlane" : qUnion([Q0])});
            skLineSegment(sketch, "E41.0", {"start": v(16.09, -4.05) * mm, "end": v(20, -4.05) * mm});
            skLineSegment(sketch, "E41.3", {"start": v(20, -4.05) * mm, "end": v(20, -5.65) * mm});
            skArc(sketch, "E41.4", {"start": v(20, -5.65) * mm, "mid": v(21.6, -6.05) * mm, "end": v(23.2, -5.65) * mm});
            skLineSegment(sketch, "E41.5", {"start": v(23.2, -5.65) * mm, "end": v(26.09, -5.65) * mm});
            skLineSegment(sketch, "E41.7", {"start": v(24.82, -8.05) * mm, "end": v(16.07, -8.05) * mm, "construction": true});
            skLineSegment(sketch, "E42", {"start": v(26.09, -5.65) * mm, "end": v(26.09, -8.65) * mm});
            skLineSegment(sketch, "E43", {"start": v(26.09, -8.65) * mm, "end": v(16.09, -8.65) * mm});
            skLineSegment(sketch, "E44", {"start": v(16.09, -8.65) * mm, "end": v(16.09, -4.05) * mm});
            skPoint(sketch, "E45.orphan", {"position": v(3, -4.05) * mm});
            skSolve(sketch);
        }
        {
            var Q0;
            Q0=qSketchRegion(id+"F28",true);
            var Q1;
            Q1=makeQuery(id+"F8.opRevolve","SWEPT_EDGE",EDGE,{"disambiguationData":[OSD([sQuery(id+"F7.wireOp",EDGE,"E8.bottom"),sQuery(id+"F7.wireOp",EDGE,"E8.right")])]});
            revolve(context, id + "F29", {"operationType" : NewBodyOperationType.ADD, "entities" : qUnion([Q0]), "axis" : qUnion([Q1]), "revolveType" : RevolveType.FULL});
        }
        {
            var Q0;
            {var subQ0=sQuery(id+"F10.wireOp",EDGE,"E13.0.3");var subQ1=sQuery(id+"F10.wireOp",EDGE,"E13.0.2");var subQ2=sQuery(id+"F10.wireOp",EDGE,"E13.0.1");var subQ3=sQuery(id+"F10.wireOp",EDGE,"E13.0.0");Q0=makeQuery(id+"F29.boolean.opBoolean","INTERSECT",EDGE,{"derivedFrom":[makeQuery(id+"F27.boolean.opBoolean","MERGE",FACE,{"derivedFrom":[makeQuery(id+"F12.opBoolean","SPLIT",FACE,{"disambiguationData":[TD([makeQuery(id+"F2.opExtrude","SWEPT_FACE",FACE,{"disambiguationData":[OSD([sQuery(id+"F1.wireOp",EDGE,"E3.0")])]})])],"derivedFrom":makeQuery(id+"F11.opExtrude","CAP_FACE",FACE,{"disambiguationData":[OSD([subQ3,subQ2,subQ1,subQ0])],"isStart":true})}),makeQuery(id+"F27.opExtrude","CAP_FACE",FACE,{"disambiguationData":[OSD([subQ3,subQ2,subQ1,subQ0])],"isStart":false})]}),makeQuery(id+"F29.opRevolve","SWEPT_FACE",FACE,{"disambiguationData":[OSD([sQuery(id+"F28.wireOp",EDGE,"E43")])]})]});}
            chamfer(context, id + "F30", {"entities" : qUnion([Q0]), "chamferType" : ChamferType.OFFSET_ANGLE, "width" : 2.8 * mm, "oppositeDirection" : false, "angle" : 45 * degree, "tangentPropagation" : true});
        }
        {
            var Q0;
            Q0=makeQuery(id+"F29.opRevolve","SWEPT_FACE",FACE,{"disambiguationData":[OSD([sQuery(id+"F28.wireOp",EDGE,"E42")])]});
            var sketch = newSketch(context, id + "F31", { "sketchPlane" : qUnion([Q0])});
            skCircle(sketch, "E46.0.0", {"center": v(0, 0) * mm, "radius": 8.65 * mm});
            skSolve(sketch);
        }
        {
            var Q0;
            Q0=makeQuery(id+"F31.imprint","IMPRINT",FACE,{"disambiguationData":[TD([[makeQuery(id+"F31.imprint","IMPRINT",EDGE,{"derivedFrom":sQuery(id+"F31.wireOp",EDGE,"E46.0.0")}),-1.0]])]});
            var Q1;
            Q1=makeQuery(id+"F31.imprint","IMPRINT",FACE,{"disambiguationData":[TD([[makeQuery(id+"F31.imprint","IMPRINT",EDGE,{"derivedFrom":makeQuery(id+"F29.boolean.opBoolean","MERGE",EDGE,{"derivedFrom":[makeQuery(id+"F8.opRevolve","SWEPT_EDGE",EDGE,{"disambiguationData":[OSD([sQuery(id+"F7.wireOp",EDGE,"E10"),sQuery(id+"F7.wireOp",EDGE,"E11.0")])]}),makeQuery(id+"F29.opRevolve","SWEPT_EDGE",EDGE,{"disambiguationData":[OSD([sQuery(id+"F28.wireOp",EDGE,"E41.5"),sQuery(id+"F28.wireOp",EDGE,"E42")])]})]})}),-1.0]])]});
            extrude(context, id + "F32", {"entities" : qUnion([Q0, Q1]), "operationType" : NewBodyOperationType.REMOVE, "oppositeDirection" : true, "depth" : 1.5 * mm});
        }
        {
            var Q0;
            Q0=makeQuery(id+"F29.boolean.opBoolean","MERGE",EDGE,{"derivedFrom":[makeQuery(id+"F8.opRevolve","SWEPT_EDGE",EDGE,{"disambiguationData":[OSD([sQuery(id+"F7.wireOp",EDGE,"E10"),sQuery(id+"F7.wireOp",EDGE,"E11.0")])]}),makeQuery(id+"F29.opRevolve","SWEPT_EDGE",EDGE,{"disambiguationData":[OSD([sQuery(id+"F28.wireOp",EDGE,"E41.5"),sQuery(id+"F28.wireOp",EDGE,"E42")])]})]});
            var Q1;
            Q1=makeQuery(id+"F32.boolean.opBoolean","INTERSECT",EDGE,{"derivedFrom":[makeQuery(id+"F8.opRevolve","SWEPT_FACE",FACE,{"disambiguationData":[OSD([sQuery(id+"F7.wireOp",EDGE,"E10")])]}),makeQuery(id+"F32.opExtrude","CAP_FACE",FACE,{"disambiguationData":[OSD([sQuery(id+"F31.wireOp",EDGE,"E46.0.0")])],"isStart":false})]});
            fillet(context, id + "F33", {"entities" : qUnion([Q0, Q1]), "radius" : .8 * mm, "tangentPropagation" : true, "allowEdgeOverflow" : false});
        }
        {
            var Q0;
            Q0=makeQuery(id+"F32.boolean.opBoolean","COPY",FACE,{"derivedFrom":makeQuery(id+"F32.opExtrude","CAP_FACE",FACE,{"disambiguationData":[OSD([sQuery(id+"F31.wireOp",EDGE,"E46.0.0")])],"isStart":false})});
            var sketch = newSketch(context, id + "F34", { "sketchPlane" : qUnion([Q0])});
            skLineSegment(sketch, "E47.bottom", {"start": v(-5, 0.25) * mm, "end": v(-15, 0.25) * mm});
            skLineSegment(sketch, "E47.top", {"start": v(-5, -0.25) * mm, "end": v(-15, -0.25) * mm});
            skLineSegment(sketch, "E47.left", {"start": v(-5, 0.25) * mm, "end": v(-5, -0.25) * mm});
            skLineSegment(sketch, "E47.right", {"start": v(-15, 0.25) * mm, "end": v(-15, -0.25) * mm});
            skPoint(sketch, "E47.middle", {"position": v(-10, 0) * mm});
            skSolve(sketch);
        }
        {
            var Q0;
            Q0=qSketchRegion(id+"F34",true);
            var Q1;
            Q1=makeQuery(id+"F8.opRevolve","SWEPT_FACE",FACE,{"disambiguationData":[OSD([sQuery(id+"F7.wireOp",EDGE,"E8.right")])]});
            extrude(context, id + "F35", {"entities" : qUnion([Q0]), "operationType" : NewBodyOperationType.REMOVE, "endBound" : BoundingType.UP_TO_SURFACE, "oppositeDirection" : true, "endBoundEntityFace" : qUnion([Q1]), "depth" : 25 * mm});
        }
        {
            var Q0;
            {var subQ0=sQuery(id+"F1.wireOp",EDGE,"E4.3");var subQ1=sQuery(id+"F1.wireOp",EDGE,"E4.2");var subQ2=sQuery(id+"F1.wireOp",EDGE,"E4.1");var subQ3=sQuery(id+"F1.wireOp",EDGE,"E4.0");var subQ4=sQuery(id+"F1.wireOp",EDGE,"E3.0");var subQ5=sQuery(id+"F1.wireOp",EDGE,"E3.3");var subQ6=sQuery(id+"F1.wireOp",EDGE,"E3.1");var subQ7=sQuery(id+"F1.wireOp",EDGE,"E3.2");Q0=makeQuery(id+"F16.boolean.opBoolean","SPLIT",FACE,{"disambiguationData":[TD([makeQuery(id+"F2.opExtrude","SWEPT_FACE",FACE,{"disambiguationData":[OSD([subQ4])]})])],"derivedFrom":makeQuery(id+"F4.boolean.opBoolean","MERGE",FACE,{"derivedFrom":[makeQuery(id+"F2.opExtrude","CAP_FACE",FACE,{"disambiguationData":[OSD([subQ4,subQ6,subQ7,subQ5,subQ3,subQ2,subQ1,subQ0])],"isStart":true}),makeQuery(id+"F4.opExtrude","CAP_FACE",FACE,{"disambiguationData":[OSD([sQuery(id+"F3.wireOp",EDGE,"E6.0.0"),sQuery(id+"F3.wireOp",EDGE,"E6.0.1"),sQuery(id+"F3.wireOp",EDGE,"E6.0.2"),sQuery(id+"F3.wireOp",EDGE,"E6.0.3")])],"isStart":true})]})});}
            var sketch = newSketch(context, id + "F36", { "sketchPlane" : qUnion([Q0])});
            skLineSegment(sketch, "E48", {"start": v(-17.68, 17.68) * mm, "end": v(0, 0) * mm, "construction": true});
            skLineSegment(sketch, "E49", {"start": v(-12.36, 11.65) * mm, "end": v(-8.11, 7.4) * mm});
            skLineSegment(sketch, "E50", {"start": v(-8.11, 7.4) * mm, "end": v(-7.4, 8.11) * mm});
            skLineSegment(sketch, "E51", {"start": v(-7.4, 8.11) * mm, "end": v(-11.65, 12.36) * mm});
            skLineSegment(sketch, "E52", {"start": v(-11.65, 12.36) * mm, "end": v(-12.36, 11.65) * mm});
            skSolve(sketch);
        }
        {
            var Q0;
            Q0 = qSketchRegion(id + "F36", true);
            var Q1;
            {var subQ0=sQuery(id+"F23.wireOp",EDGE,"E35.bottom");Q1=makeQuery(id+"F6eMsZc8lIHEnnu_1.3.F24.boolean.opBoolean","MERGE",FACE,{"derivedFrom":[makeQuery(id+"F6eMsZc8lIHEnnu_1.2.F24.boolean.opBoolean","MERGE",FACE,{"derivedFrom":[makeQuery(id+"F6eMsZc8lIHEnnu_1.1.F24.boolean.opBoolean","MERGE",FACE,{"derivedFrom":[makeQuery(id+"F24.boolean.opBoolean","MERGE",FACE,{"derivedFrom":[makeQuery(id+"F12.opBoolean","SPLIT",FACE,{"disambiguationData":[TD([makeQuery(id+"F2.opExtrude","SWEPT_FACE",FACE,{"disambiguationData":[OSD([sQuery(id+"F1.wireOp",EDGE,"E3.0")])]})])],"derivedFrom":makeQuery(id+"F11.opExtrude","CAP_FACE",FACE,{"disambiguationData":[OSD([sQuery(id+"F10.wireOp",EDGE,"E13.0.0"),sQuery(id+"F10.wireOp",EDGE,"E13.0.1"),sQuery(id+"F10.wireOp",EDGE,"E13.0.2"),sQuery(id+"F10.wireOp",EDGE,"E13.0.3")])],"isStart":false})}),makeQuery(id+"F24.opExtrude","SWEPT_FACE",FACE,{"disambiguationData":[OSD([subQ0])]})]}),makeQuery(id+"F6eMsZc8lIHEnnu_1.1.F24.opExtrude","SWEPT_FACE",FACE,{"disambiguationData":[OSD([subQ0])]})]}),makeQuery(id+"F6eMsZc8lIHEnnu_1.2.F24.opExtrude","SWEPT_FACE",FACE,{"disambiguationData":[OSD([subQ0])]})]}),makeQuery(id+"F6eMsZc8lIHEnnu_1.3.F24.opExtrude","SWEPT_FACE",FACE,{"disambiguationData":[OSD([subQ0])]})]});}
            extrude(context, id + "F37", {"entities" : qUnion([Q0]), "operationType" : NewBodyOperationType.REMOVE, "endBound" : BoundingType.UP_TO_SURFACE, "oppositeDirection" : true, "endBoundEntityFace" : qUnion([Q1]), "depth" : 25 * mm});
        }
    });
